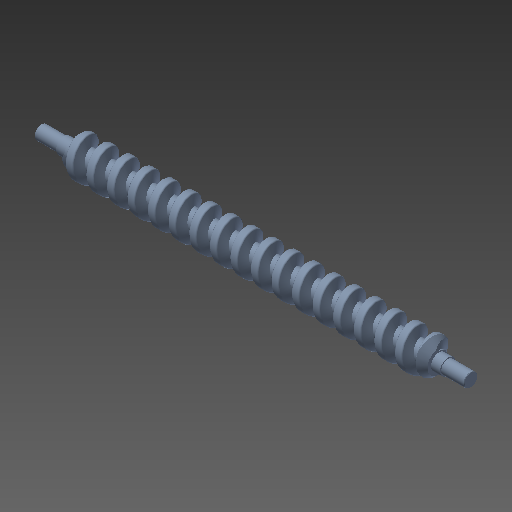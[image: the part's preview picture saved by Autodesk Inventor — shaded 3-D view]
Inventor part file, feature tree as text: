
AUTODESK INVENTOR PART (.ipt)
format: ipt  version: 2020 (Build 240168000, 168)  size: 965,632 bytes
history: native  units: mm
features: revolve x2, mirror x2, other x1, chamfer x1, helix x1, fillet x1, sketch x1
ambient origin geometry x8: Origin, YZ Plane, XZ Plane, XY Plane, X Axis, Y Axis, Z Axis, Center Point
bodies: Body1 (feature_tree)
feature tree (9):
  other  "實體1"
  revolve  "Revolution1"  [1 undecoded]
  mirror  "Mirror1"
  chamfer  "Chamfer2"  Distance=1.75mm
  helix  "Coil3"  [1 undecoded]
  revolve  "Revolution2"  [1 undecoded]
  mirror  "Mirror2"
  fillet  "Fillet5"  [1 undecoded]
  sketch  "Sketch6"  dims[d0=2.0mm d1=40.0mm d4=1.75mm d5=1.5mm d7=5.0mm d8=90.0deg d38=0.1mm d39=2.0mm d40=45.0deg d43=2.0mm d54=2.0mm d57=3.490659mm d58=1.5mm d59=3.0mm d60=4.5mm d61=10.0mm d62=190.0mm d63=0.0mm d64=90.0deg d65=90.0deg d66=0.0mm d67=0.0mm d72=45.0deg d73=2.5mm d74=90.0deg d75=3.0mm d76=0.3mm d77=2.27206mm d78=4.0mm d79=2.0mm]
note: 4 required parameter values undecoded (feature->parameter linkage not recoverable at this tier; creation-order binding heuristic only, values carry confidence <= 0.55)